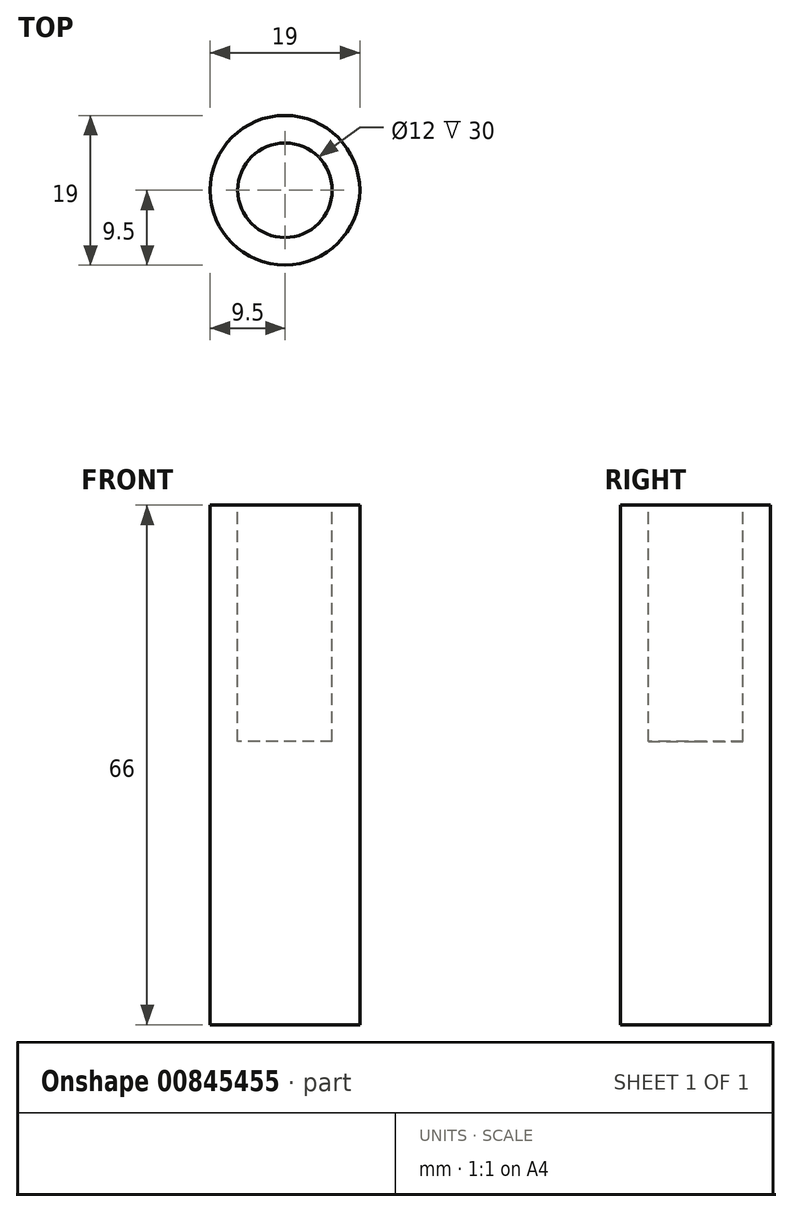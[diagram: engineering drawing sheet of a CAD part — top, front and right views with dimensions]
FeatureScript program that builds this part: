
annotation { "Feature Type Name" : "Feature", "Feature Type Description" : "" }
export const myFeature = defineFeature(function(context is Context, id is Id, definition is map)
    precondition{}
    {
        {
            var Q0;
            Q0=qCreatedBy(makeId("Top.planeOp"),FACE);
            var sketch = newSketch(context, id + "F0", { "sketchPlane" : qUnion([Q0])});
            skCircle(sketch, "E0", {"center": v(0, 0) * mm, "radius": 9.5 * mm});
            skSolve(sketch);
        }
        {
            var Q0;
            Q0 = qSketchRegion(id + "F0", true);
            extrude(context, id + "F1", {"entities" : qUnion([Q0]), "oppositeDirection" : true, "depth" : 66 * mm, "offsetDistance" : 25 * mm});
        }
        {
            var Q0;
            Q0=qCreatedBy(makeId("Top.planeOp"),FACE);
            var sketch = newSketch(context, id + "F2", { "sketchPlane" : qUnion([Q0])});
            skCircle(sketch, "E1", {"center": v(0, 0) * mm, "radius": 6 * mm});
            skSolve(sketch);
        }
        {
            var Q0;
            Q0=makeQuery(id+"F2.imprint","IMPRINT",FACE,{"disambiguationData":[TD([[makeQuery(id+"F2.imprint","IMPRINT",EDGE,{"derivedFrom":sQuery(id+"F2.wireOp",EDGE,"E1")}),1.0]])]});
            extrude(context, id + "F3", {"entities" : qUnion([Q0]), "operationType" : NewBodyOperationType.REMOVE, "oppositeDirection" : true, "depth" : 30 * mm, "offsetDistance" : 25 * mm});
        }
    });
